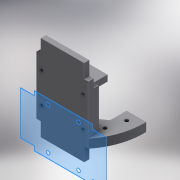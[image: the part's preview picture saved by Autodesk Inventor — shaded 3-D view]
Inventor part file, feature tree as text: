
AUTODESK INVENTOR PART (.ipt)
format: ipt  version: 2017 (Build 210142000, 142)  size: 418,304 bytes
history: native  units: mm
features: sketch x10, extrude x7, projected_geometry x6, other x3, hole x2, mirror x2, revolve x1, reference x1
ambient origin geometry x8: Origin, YZ Plane, XZ Plane, XY Plane, X Axis, Y Axis, Z Axis, Center Point
bodies: Solid1 (feature_tree), Solid2 (feature_tree)
feature tree (32):
  extrude  "Extrusion1"  Depth=60.0mm
  extrude  "Extrusion2"  Depth=16.0mm
  hole  "Hole1"  [1 undecoded]
  extrude  "Extrusion3"  Depth=6.0mm
  extrude  "Extrusion4"  Depth=6.0mm
  mirror  "Mirror1"
  extrude  "Extrusion5"  Depth=6.0mm TaperAngle=0.0deg
  mirror  "Mirror2"
  sketch  "Sketch8"  dims[d13=4.2mm d14=6.0mm d15=4.0mm d16=2.0mm d17=90.0deg d18=8.0mm d19=20.594885mm d20=6.0mm d21=0.0mm]
  extrude  "Extrusion6"  Depth=10.0mm
  revolve  "Revolution1"  [1 undecoded]
  hole  "Hole2"  [1 undecoded]
  extrude  "Extrusion7"  Depth=7.2mm
  sketch  "Sketch1"  dims[d0=47.0mm d1=60.0mm]
  sketch  "Sketch2"  dims[d2=6.0mm d3=0.0mm d4=16.0mm]
  projected_geometry  "Projected Loop1"
  sketch  "Sketch3"  dims[d5=7.0mm d6=30.0mm]
  projected_geometry  "Projected Loop2"
  projected_geometry  "Projected Loop3"
  sketch  "Sketch4"  dims[d7=60.0mm d8=0.0mm d9=6.0mm]
  projected_geometry  "Projected Loop4"
  sketch  "Sketch5"  dims[d10=6.0mm d11=6.0mm]
  reference  "Reference1"
  sketch  "Sketch6"  dims[d12=6.0mm]
  projected_geometry  "Projected Loop5"
  sketch  "Sketch9"  dims[d25=10.0mm d26=50.0mm]
  projected_geometry  "Projected Loop6"
  sketch  "Sketch10"  dims[d27=5.0mm d28=16.0mm]
  sketch  "Sketch11"  dims[d29=10.0mm d30=0.0mm d31=7.2mm d32=7.2mm d33=7.2mm d34=4.0mm d35=0.0mm d36=19.0mm d37=45.0deg d38=40.0mm d40=360.0deg d42=16.0mm d43=0.0mm d44=90.0deg d45=30.0mm d46=4.25mm d47=6.0mm d48=8.0mm d49=6.0mm d50=90.0deg d51=8.0mm d52=20.594885mm d53=7.2mm d54=7.2mm d55=7.2mm d56=7.2mm d57=7.25mm d58=0.0mm]
  other  "<userpath>\Dropbox\Work\Project\Inventor\Right shoulder.iam"
  other  "Right shoulder.iam"
  other  "Arm - right shoulder v3:1"
note: 3 required parameter values undecoded (feature->parameter linkage not recoverable at this tier; creation-order binding heuristic only, values carry confidence <= 0.55)